FCSTD DOCUMENT  (FreeCAD 0.21R33771 (Git))
Label: 二代底盘
License: All rights reserved
LicenseURL: http://en.wikipedia.org/wiki/All_rights_reserved
objects: Sketcher::SketchObject×1
note: 1 computed .brp shape members not serialized (recipe doc carries the construction recipe); baked Part::Feature solids carry a one-line shape summary decoded from their .brp

FEATURE [Sketcher::SketchObject] Sketch
  FullyConstrained = true
  sketch-geometry (34):
    g0: Circle CenterX=-40 CenterY=0 CenterZ=0 NormalX=0 NormalY=0 NormalZ=1 AngleXU=0 Radius=1.75
    g1: Circle CenterX=40 CenterY=0 CenterZ=0 NormalX=0 NormalY=0 NormalZ=1 AngleXU=0 Radius=1.75
    g2: Circle CenterX=-9.5 CenterY=38 CenterZ=0 NormalX=0 NormalY=0 NormalZ=1 AngleXU=0 Radius=1.75
    g3: Circle CenterX=9.5 CenterY=38 CenterZ=0 NormalX=0 NormalY=0 NormalZ=1 AngleXU=0 Radius=1.75
    g4: Circle CenterX=-40 CenterY=-85 CenterZ=0 NormalX=0 NormalY=0 NormalZ=1 AngleXU=0 Radius=1.75
    g5: Circle CenterX=40 CenterY=-85 CenterZ=0 NormalX=0 NormalY=0 NormalZ=1 AngleXU=0 Radius=1.75
    g6: Circle CenterX=-44 CenterY=-135 CenterZ=0 NormalX=0 NormalY=0 NormalZ=1 AngleXU=0 Radius=1.75
    g7: Circle CenterX=-44 CenterY=-151 CenterZ=0 NormalX=0 NormalY=0 NormalZ=1 AngleXU=0 Radius=1.75
    g8: Circle CenterX=-58 CenterY=-135 CenterZ=0 NormalX=0 NormalY=0 NormalZ=1 AngleXU=0 Radius=1.75
    g9: Circle CenterX=-58 CenterY=-151 CenterZ=0 NormalX=0 NormalY=0 NormalZ=1 AngleXU=0 Radius=1.75
    g10: Circle CenterX=44 CenterY=-135 CenterZ=0 NormalX=0 NormalY=0 NormalZ=1 AngleXU=0 Radius=1.75
    g11: Circle CenterX=58 CenterY=-135 CenterZ=0 NormalX=0 NormalY=0 NormalZ=1 AngleXU=0 Radius=1.75
    g12: Circle CenterX=44 CenterY=-151 CenterZ=0 NormalX=0 NormalY=0 NormalZ=1 AngleXU=0 Radius=1.75
    g13: Circle CenterX=58 CenterY=-151 CenterZ=0 NormalX=0 NormalY=0 NormalZ=1 AngleXU=0 Radius=1.75
    g14: LineSegment StartX=-14 StartY=46 StartZ=0 EndX=14 EndY=46 EndZ=0
    g15: LineSegment StartX=-59.4761 StartY=-159 StartZ=0 EndX=57.4139 EndY=-159 EndZ=0
    g16: LineSegment StartX=-50 StartY=8 StartZ=0 EndX=-50 EndY=-95 EndZ=0
    g17: LineSegment StartX=50 StartY=8 StartZ=0 EndX=50 EndY=-95 EndZ=0
    g18: LineSegment StartX=-64.4761 StartY=-125 StartZ=0 EndX=-64.4761 EndY=-154 EndZ=0
    g19: LineSegment StartX=62.4139 StartY=-125 StartZ=0 EndX=62.4139 EndY=-154 EndZ=0
    g20: ArcOfCircle CenterX=-59.4761 CenterY=-154 CenterZ=0 NormalX=0 NormalY=0 NormalZ=1 AngleXU=0 Radius=5 StartAngle=3.14159 EndAngle=4.71239
    g21: ArcOfCircle CenterX=57.4139 CenterY=-154 CenterZ=0 NormalX=0 NormalY=0 NormalZ=1 AngleXU=0 Radius=5 StartAngle=4.71239 EndAngle=6.28319
    g22: LineSegment StartX=-50 StartY=-95 StartZ=0 EndX=-64.4761 EndY=-125 EndZ=0
    g23: LineSegment StartX=50 StartY=-95 StartZ=0 EndX=62.4139 EndY=-125 EndZ=0
    g24: LineSegment StartX=-30 StartY=30 StartZ=0 EndX=-30 EndY=20 EndZ=0
    g25: LineSegment StartX=30 StartY=30 StartZ=0 EndX=30 EndY=20 EndZ=0
    g26: LineSegment StartX=-50 StartY=8 StartZ=0 EndX=-30 EndY=20 EndZ=0
    g27: LineSegment StartX=30 StartY=20 StartZ=0 EndX=50 EndY=8 EndZ=0
    g28: ArcOfCircle CenterX=-14 CenterY=30 CenterZ=0 NormalX=0 NormalY=0 NormalZ=1 AngleXU=0 Radius=16 StartAngle=1.5708 EndAngle=3.14159
    g29: ArcOfCircle CenterX=14 CenterY=30 CenterZ=0 NormalX=0 NormalY=0 NormalZ=1 AngleXU=0 Radius=16 StartAngle=0 EndAngle=1.5708
    g30: LineSegment StartX=-13 StartY=-5 StartZ=0 EndX=13 EndY=-5 EndZ=0
    g31: LineSegment StartX=13 StartY=-5 StartZ=0 EndX=13 EndY=-15 EndZ=0
    g32: LineSegment StartX=13 StartY=-15 StartZ=0 EndX=-13 EndY=-15 EndZ=0
    g33: LineSegment StartX=-13 StartY=-15 StartZ=0 EndX=-13 EndY=-5 EndZ=0
  constraints (91):
    c: Radius(g0) = 1.75
    c: Radius(g1) = 1.75
    c: Symmetric(g0,g1,g-2)
    c: PointOnObject(g0,g-1)
    c: DistanceX(g0,g1) = 80
    c: Radius(g2) = 1.75
    c: Radius(g3) = 1.75
    c: Symmetric(g2,g3,g-2)
    c: DistanceX(g2,g3) = 19
    c: DistanceY(g0,g2) = 38
    c: Radius(g4) = 1.75
    c: Radius(g5) = 1.75
    c: Symmetric(g4,g5,g-2)
    c: DistanceX(g4,g5) = 80
    c: DistanceY(g5,g1) = 85
    c: Equal(g6,g7)
    c: Equal(g6,g8)
    c: Equal(g6,g9)
    c: Radius(g6) = 1.75
    c: Equal(g10,g11)
    c: Equal(g10,g12)
    c: Equal(g10,g13)
    c: Radius(g10) = 1.75
    c: Symmetric(g6,g10,g-2)
    c: Symmetric(g8,g11,g-2)
    c: Symmetric(g7,g12,g-2)
    c: Symmetric(g9,g13,g-2)
    c: Horizontal(g8,g6)
    c: Horizontal(g9,g7)
    c: Vertical(g8,g9)
    c: Vertical(g6,g7)
    c: DistanceX(g8,g6) = 14
    c: DistanceY(g9,g8) = 16
    c: DistanceX(g6,g10) = 88
    c: DistanceY(g10,g5) = 50
    c: Horizontal(g14)
    c: Horizontal(g15)
    c: Vertical(g16)
    c: Vertical(g17)
    c: Vertical(g18)
    c: Vertical(g19)
    c: Tangent(g18,g20) = -1.5708
    c: Tangent(g15,g20) = -1.5708
    c: Tangent(g15,g21) = -1.5708
    c: Tangent(g19,g21) = 1.5708
    c: DistanceX(g16,g4) = 10
    c: DistanceX(g5,g17) = 10
    c: Coincident(g22,g16)
    c: Coincident(g22,g18)
    c: Coincident(g23,g17)
    c: Coincident(g23,g19)
    c: DistanceY(g8,g18) = 10
    c: DistanceY(g11,g19) = 10
    c: DistanceY(g16,g4) = 10
    c: DistanceY(g17,g5) = 10
    c: DistanceY(g0,g16) = 8
    c: DistanceY(g1,g17) = 8
    c: Vertical(g24)
    c: Vertical(g25)
    c: DistanceY(g16,g24) = 12
    c: DistanceY(g17,g25) = 12
    c: DistanceX(g24,g-1) = 30
    c: DistanceX(g-1,g25) = 30
    c: Coincident(g26,g24)
    c: Coincident(g26,g16)
    c: Coincident(g27,g17)
    c: Coincident(g27,g25)
    c: Tangent(g24,g28) = -1.5708
    c: Tangent(g14,g28) = 1.5708
    c: Tangent(g25,g29) = 1.5708
    c: Tangent(g14,g29) = 1.5708
    c: DistanceY(g2,g14) = 8
    c: Radius(g28) = 16
    c: Radius(g29) = 16
    c: Radius(g20) = 5
    c: Radius(g21) = 5
    c: DistanceY(g15,g9) = 8
    c: DistanceX(g15,g15) = 116.89
    c: Distance(g22) = 33.31
    c: Coincident(g30,g31)
    c: Coincident(g31,g32)
    c: Coincident(g32,g33)
    c: Coincident(g33,g30)
    c: Horizontal(g30)
    c: Horizontal(g32)
    c: Vertical(g31)
    c: Vertical(g33)
    c: DistanceX(g30,g30) = 26
    c: DistanceY(g31,g31) = 10
    c: DistanceY(g30,g0) = 5
    c: DistanceX(g30,g-1) = 13
